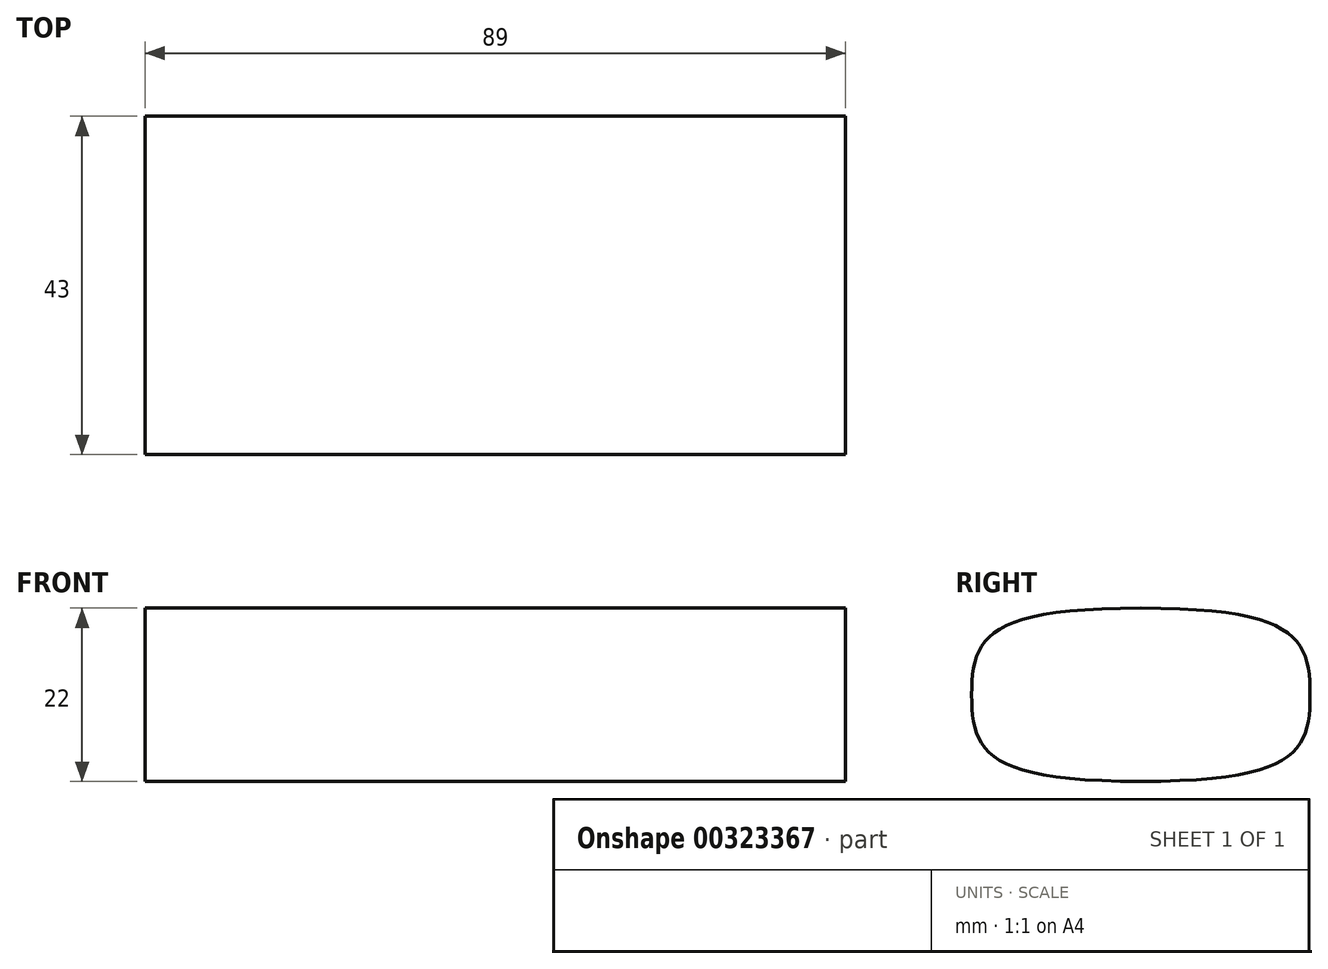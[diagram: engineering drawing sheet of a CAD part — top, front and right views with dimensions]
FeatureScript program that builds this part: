
annotation { "Feature Type Name" : "Feature", "Feature Type Description" : "" }
export const myFeature = defineFeature(function(context is Context, id is Id, definition is map)
    precondition{}
    {
        {
            var Q0;
            Q0=qCreatedBy(makeId("Top.planeOp"),FACE);
            var sketch = newSketch(context, id + "F0", { "sketchPlane" : qUnion([Q0])});
            skLineSegment(sketch, "E0.bottom", {"start": v(0, 0) * mm, "end": v(89, 0) * mm});
            skLineSegment(sketch, "E0.top", {"start": v(0, 43) * mm, "end": v(89, 43) * mm});
            skLineSegment(sketch, "E0.left", {"start": v(0, 0) * mm, "end": v(0, 43) * mm});
            skLineSegment(sketch, "E0.right", {"start": v(89, 0) * mm, "end": v(89, 43) * mm});
            skSolve(sketch);
        }
        {
            var Q0;
            Q0=makeQuery(id+"F0.imprint","IMPRINT",FACE,{"disambiguationData":[TD([[makeQuery(id+"F0.imprint","IMPRINT",EDGE,{"derivedFrom":sQuery(id+"F0.wireOp",EDGE,"E0.bottom")}),1.0]])]});
            extrude(context, id + "F1", {"entities" : qUnion([Q0]), "depth" : 22 * mm});
        }
        {
            var Q0;
            Q0=makeQuery(id+"F1.opExtrude","SWEPT_FACE",FACE,{"disambiguationData":[OSD([sQuery(id+"F0.wireOp",EDGE,"E0.right")])]});
            var sketch = newSketch(context, id + "F2", { "sketchPlane" : qUnion([Q0])});
            skLineSegment(sketch, "E1", {"start": v(0, 11) * mm, "end": v(43, 11) * mm, "construction": true});
            skLineSegment(sketch, "E2", {"start": v(21.5, 0) * mm, "end": v(21.5, 22) * mm, "construction": true});
            skFitSpline(sketch, "E3", {"points": [v(0, 11) * mm, v(1.36, 17.3) * mm, v(21.5, 22) * mm], "startDerivative": vector(0, 21.46) * mm, "endDerivative": vector(61.82, 0) * mm});
            skFitSpline(sketch, "E4.MirrorCS", {"points": [v(43, 11) * mm, v(41.64, 17.3) * mm, v(21.5, 22) * mm], "startDerivative": vector(0, 21.46) * mm, "endDerivative": vector(-61.82, 0) * mm});
            skFitSpline(sketch, "E5.MirrorCS", {"points": [v(0, 11) * mm, v(1.36, 4.7) * mm, v(21.5, 0) * mm], "startDerivative": vector(0, -21.46) * mm, "endDerivative": vector(61.82, 0) * mm});
            skFitSpline(sketch, "E6.MirrorCS", {"points": [v(43, 11) * mm, v(41.64, 4.7) * mm, v(21.5, 0) * mm], "startDerivative": vector(0, -21.46) * mm, "endDerivative": vector(-61.82, 0) * mm});
            skSolve(sketch);
        }
        {
            var Q0;
            Q0=makeQuery(id+"F2.imprint","IMPRINT",FACE,{"disambiguationData":[TD([[makeQuery(id+"F2.imprint","IMPRINT",EDGE,{"derivedFrom":sQuery(id+"F2.wireOp",EDGE,"E3")}),-1.0]])]});
            extrude(context, id + "F3", {"entities" : qUnion([Q0]), "operationType" : NewBodyOperationType.INTERSECT, "endBound" : BoundingType.THROUGH_ALL, "oppositeDirection" : true, "depth" : 25 * mm});
        }
    });
